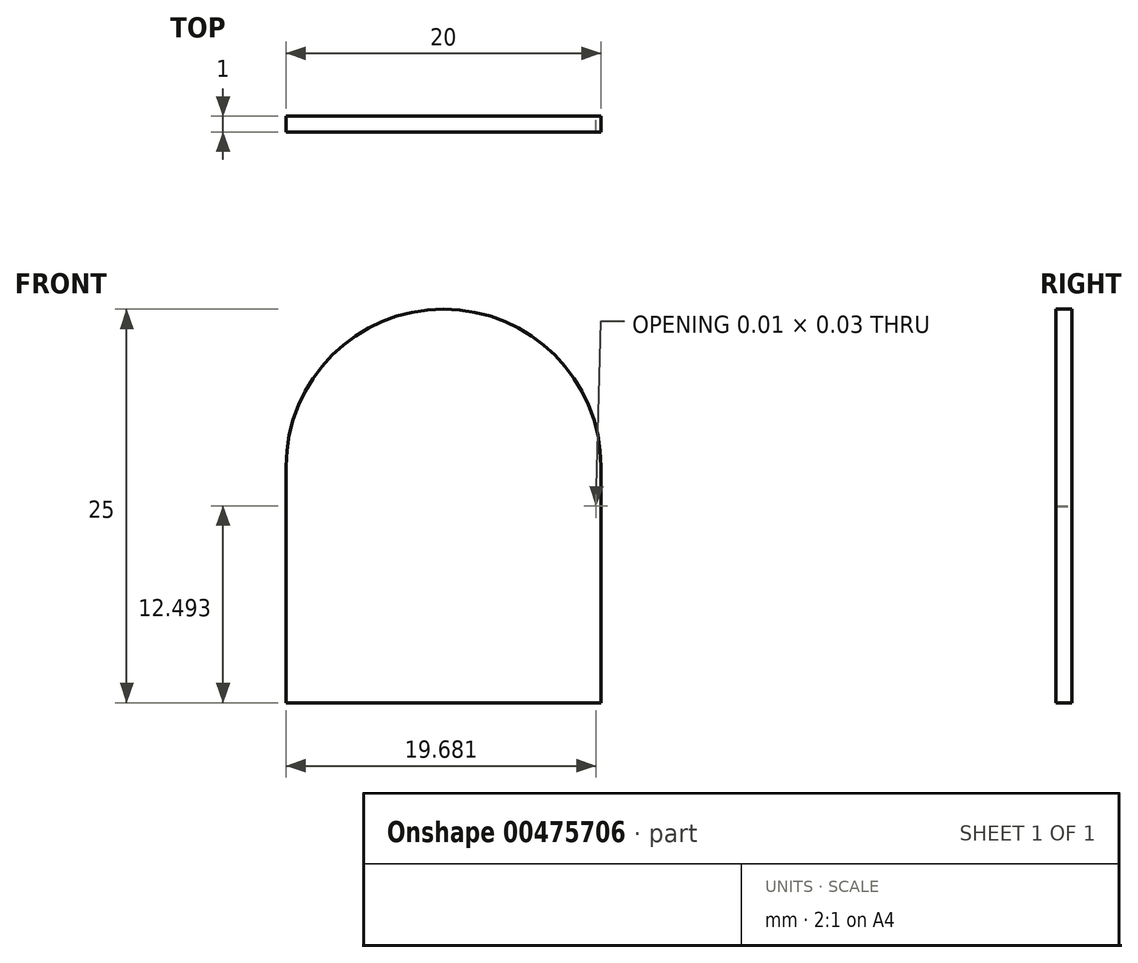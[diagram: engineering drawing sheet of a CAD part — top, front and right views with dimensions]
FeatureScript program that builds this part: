
annotation { "Feature Type Name" : "Feature", "Feature Type Description" : "" }
export const myFeature = defineFeature(function(context is Context, id is Id, definition is map)
    precondition{}
    {
        {
            var Q0;
            Q0=qCreatedBy(makeId("Front.planeOp"),FACE);
            var sketch = newSketch(context, id + "F0", { "sketchPlane" : qUnion([Q0])});
            skArc(sketch, "E0", {"start": v(9.68, -2.52) * mm, "mid": v(1.27, 9.92) * mm, "end": v(-10, 0) * mm});
            skLineSegment(sketch, "E1", {"start": v(9.68, -2.5) * mm, "end": v(9.68, -2.5) * mm});
            skPoint(sketch, "E2.end.orphan", {"position": v(-8.82, -1.93) * mm});
            skPoint(sketch, "E2.start.orphan", {"position": v(-8.82, 7.5) * mm});
            skPoint(sketch, "E3.orphan", {"position": v(1.18, -2.5) * mm});
            skLineSegment(sketch, "E4", {"start": v(9.68, -2.5) * mm, "end": v(9.68, -2.52) * mm});
            skPoint(sketch, "E5.orphan", {"position": v(-8.82, -2.5) * mm});
            skLineSegment(sketch, "E6", {"start": v(-10, 0) * mm, "end": v(-10, -15) * mm});
            skLineSegment(sketch, "E7", {"start": v(10, 0) * mm, "end": v(10, -15) * mm});
            skLineSegment(sketch, "E8", {"start": v(-10, -15) * mm, "end": v(10, -15) * mm});
            skSolve(sketch);
        }
        {
            var Q0;
            Q0 = qSketchRegion(id + "F0", true);
            extrude(context, id + "F1", {"entities" : qUnion([Q0]), "depth" : 1 * mm, "offsetDistance" : 25 * mm});
        }
    });
